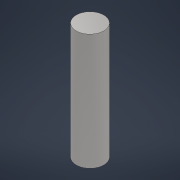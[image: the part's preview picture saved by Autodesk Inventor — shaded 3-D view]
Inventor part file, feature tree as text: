
AUTODESK INVENTOR PART (.ipt)
format: ipt  version: 2021 (Build 250183000, 183)  size: 88,064 bytes
history: native  units: mm
features: other x1, extrude x1, sketch x1
ambient origin geometry x8: Origin, YZ Plane, XZ Plane, XY Plane, X Axis, Y Axis, Z Axis, Center Point
bodies: Body1 (feature_tree)
feature tree (3):
  other  "Sólido1"
  extrude  "Extrusão1"  Depth=3.8mm TaperAngle=0.0deg
  sketch  "Esboço1"  dims[d0=0.9mm d1=3.8mm d2=0.0mm]
